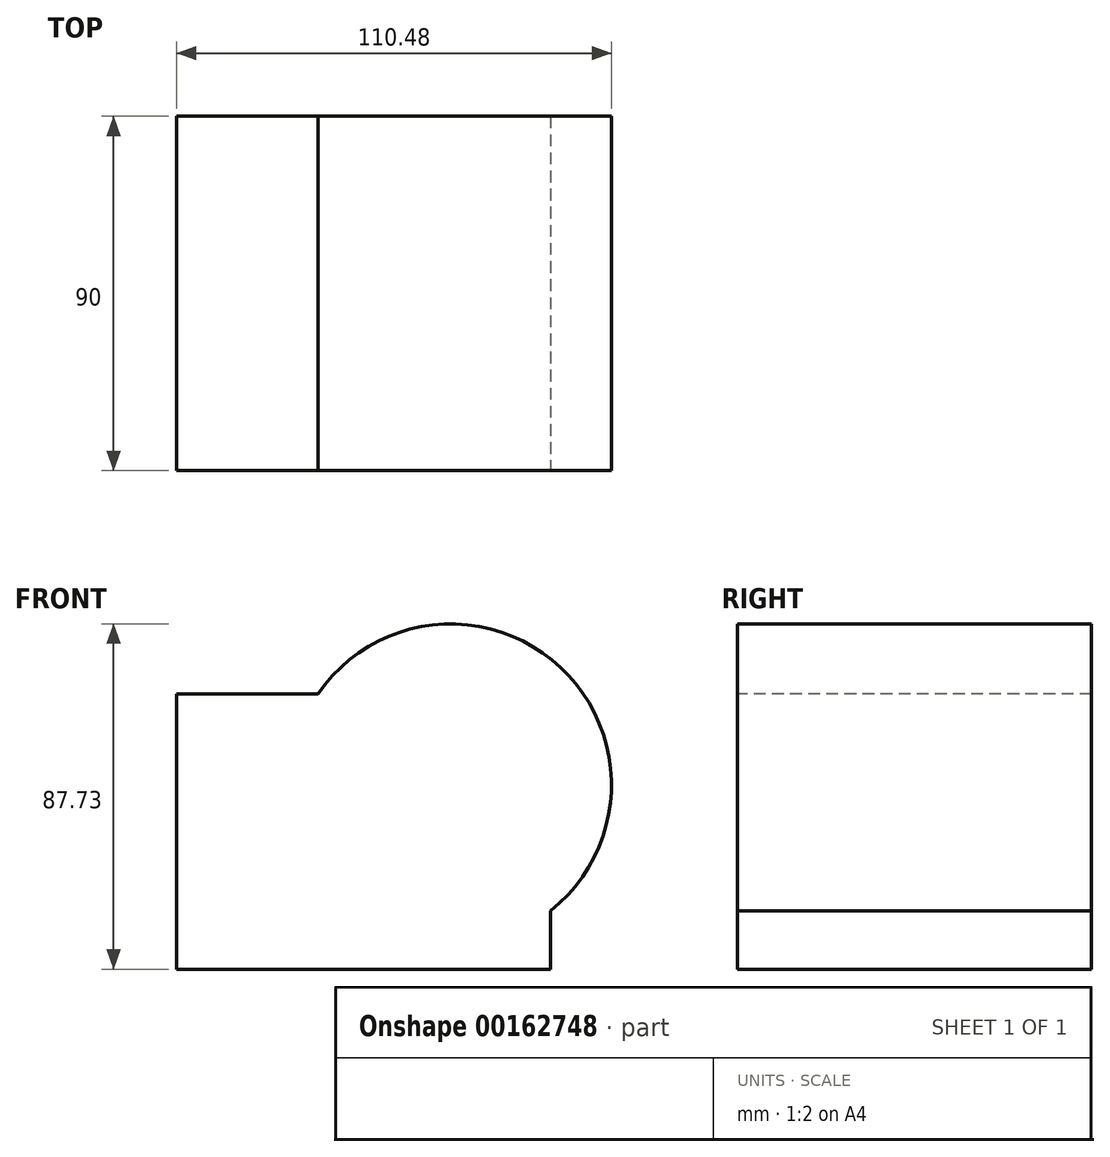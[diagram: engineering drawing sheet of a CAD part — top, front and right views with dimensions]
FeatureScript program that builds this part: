
annotation { "Feature Type Name" : "Feature", "Feature Type Description" : "" }
export const myFeature = defineFeature(function(context is Context, id is Id, definition is map)
    precondition{}
    {
        {
            var Q0;
            Q0=qCreatedBy(makeId("Top.planeOp"),FACE);
            var sketch = newSketch(context, id + "F0", { "sketchPlane" : qUnion([Q0])});
            skLineSegment(sketch, "E0.bottom", {"start": v(-50.04, 59.3) * mm, "end": v(44.96, 59.3) * mm});
            skLineSegment(sketch, "E0.top", {"start": v(-50.04, -30.7) * mm, "end": v(44.96, -30.7) * mm});
            skLineSegment(sketch, "E0.left", {"start": v(-50.04, 59.3) * mm, "end": v(-50.04, -30.7) * mm});
            skLineSegment(sketch, "E0.right", {"start": v(44.96, 59.3) * mm, "end": v(44.96, -30.7) * mm});
            skSolve(sketch);
        }
        {
            var Q0;
            Q0 = qSketchRegion(id + "F0", true);
            var Q1;
            Q1=makeQuery(id+"F0.imprint","IMPRINT",FACE,{"disambiguationData":[TD([[makeQuery(id+"F0.imprint","IMPRINT",EDGE,{"derivedFrom":sQuery(id+"F0.wireOp",EDGE,"E0.bottom")}),-1.0]])]});
            extrude(context, id + "F1", {"entities" : qUnion([Q0, Q1]), "depth" : 70 * mm});
        }
        {
            var Q0;
            Q0=makeQuery(id+"F1.opExtrude","SWEPT_FACE",FACE,{"disambiguationData":[OSD([sQuery(id+"F0.wireOp",EDGE,"E0.top")])]});
            var sketch = newSketch(context, id + "F2", { "sketchPlane" : qUnion([Q0])});
            skLineSegment(sketch, "E1", {"start": v(44.96, 46.88) * mm, "end": v(19.6, 46.88) * mm, "construction": true});
            skCircle(sketch, "E2", {"center": v(19.6, 46.88) * mm, "radius": 40.84 * mm});
            skSolve(sketch);
        }
        {
            var Q0;
            {var subQ0=sQuery(id+"F2.wireOp",EDGE,"E2");var subQ1=sQuery(id+"F0.wireOp",EDGE,"E0.top");var subQ4=makeQuery(id+"F1.opExtrude","CAP_EDGE",EDGE,{"disambiguationData":[OSD([subQ1])],"isStart":false});var subQ5=makeQuery(id+"F2.imprint","INTERSECT",VERTEX,{"derivedFrom":[subQ4,subQ0]});Q0=makeQuery(id+"F2.imprint","IMPRINT",FACE,{"disambiguationData":[TD([[makeQuery(id+"F2.imprint","IMPRINT",EDGE,{"disambiguationData":[TD([[subQ5,1.0]])],"derivedFrom":subQ0}),1.0]])]});}
            extrude(context, id + "F3", {"entities" : qUnion([Q0]), "operationType" : NewBodyOperationType.ADD, "oppositeDirection" : true, "depth" : 90 * mm});
        }
    });
